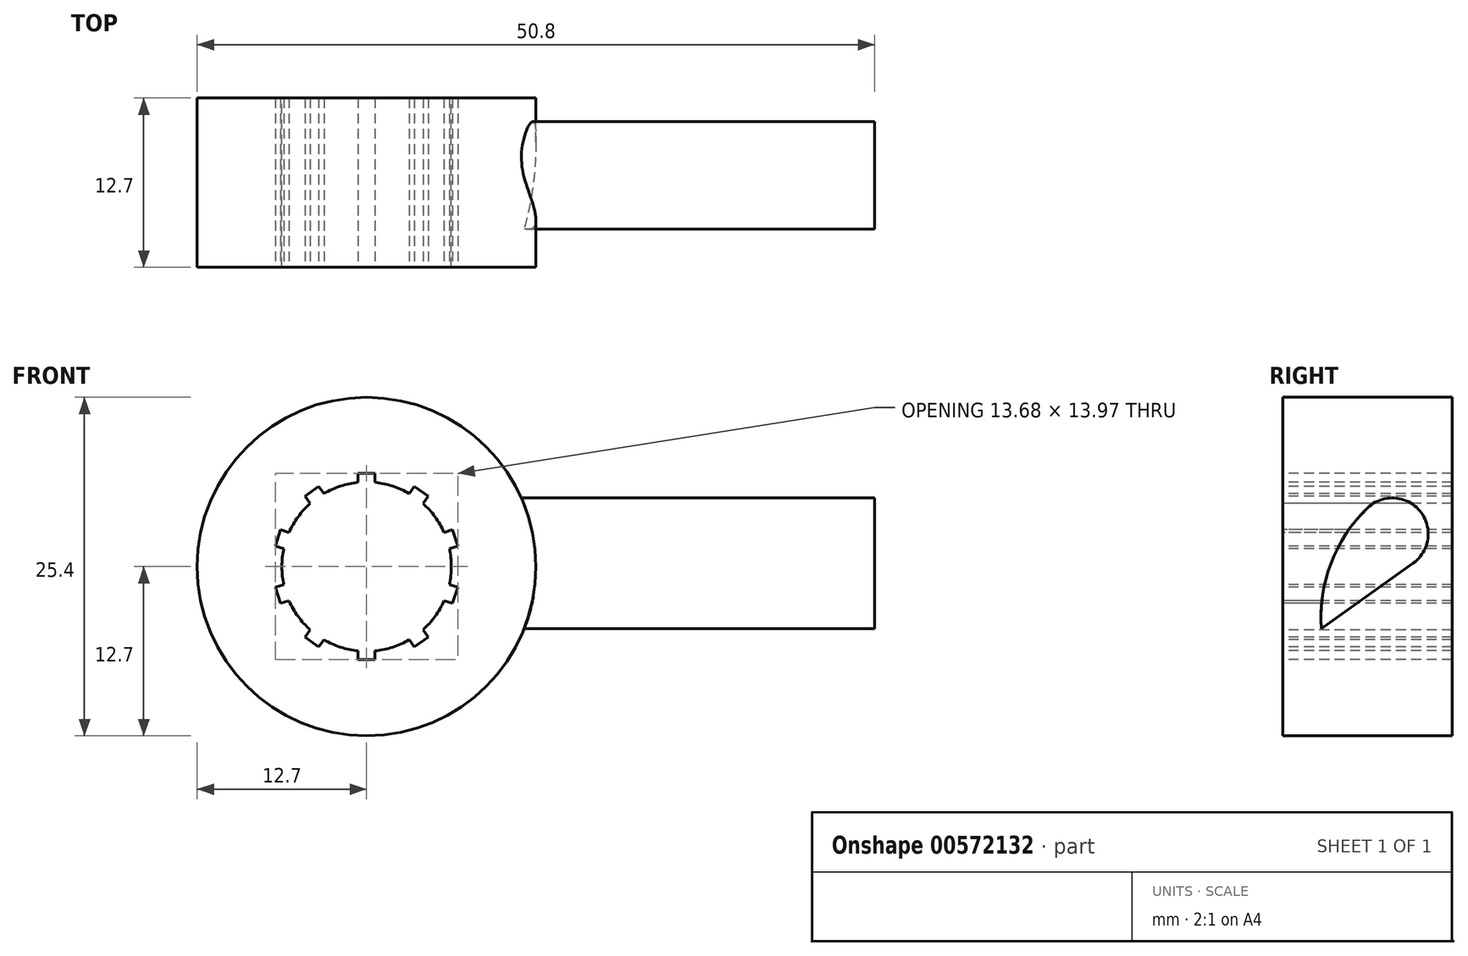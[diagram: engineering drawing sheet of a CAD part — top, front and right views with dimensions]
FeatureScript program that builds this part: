
annotation { "Feature Type Name" : "Feature", "Feature Type Description" : "" }
export const myFeature = defineFeature(function(context is Context, id is Id, definition is map)
    precondition{}
    {
        {
            var Q0;
            Q0=qCreatedBy(makeId("Front.planeOp"),FACE);
            var sketch = newSketch(context, id + "F0", { "sketchPlane" : qUnion([Q0])});
            skCircle(sketch, "E0", {"center": v(0, 0) * mm, "radius": 12.7 * mm});
            skCircle(sketch, "E1", {"center": v(0, 0) * mm, "radius": 6.35 * mm});
            skSolve(sketch);
        }
        {
            var Q0;
            Q0 = qSketchRegion(id + "F0", true);
            extrude(context, id + "F1", {"entities" : qUnion([Q0]), "endBound" : BoundingType.SYMMETRIC, "depth" : 12.7 * mm, "offsetDistance" : 25.4 * mm});
        }
        {
            var Q0;
            Q0=qCreatedBy(makeId("Front.planeOp"),FACE);
            cPlane(context, id + "F2", {"entities" : qUnion([Q0]), "cplaneType" : CPlaneType.OFFSET, "offset" : 6.35 * mm, "width" : 152.4 * mm, "height" : 152.4 * mm});
        }
        {
            var Q0;
            Q0=qCreatedBy(id+"F2.planeOp",FACE);
            var sketch = newSketch(context, id + "F3", { "sketchPlane" : qUnion([Q0])});
            skArc(sketch, "E2", {"start": v(0.63, 6.32) * mm, "mid": v(0, 6.35) * mm, "end": v(-0.64, 6.32) * mm});
            skLineSegment(sketch, "E3.bottom", {"start": v(-0.64, 6.99) * mm, "end": v(0.63, 6.99) * mm});
            skLineSegment(sketch, "E3.left", {"start": v(-0.64, 6.99) * mm, "end": v(-0.64, 6.32) * mm});
            skLineSegment(sketch, "E3.right", {"start": v(0.63, 6.99) * mm, "end": v(0.63, 6.32) * mm});
            skPoint(sketch, "E3.middle", {"position": v(0, 6.35) * mm});
            skPoint(sketch, "E3.top.start.orphan", {"position": v(-0.64, 5.72) * mm});
            skPoint(sketch, "E4.orphan", {"position": v(0.63, 5.72) * mm});
            skLineSegment(sketch, "E5.1.0", {"start": v(-3.6, 6.02) * mm, "end": v(-3.2, 5.48) * mm});
            skArc(sketch, "E5.1.1", {"start": v(-3.2, 5.48) * mm, "mid": v(-3.73, 5.14) * mm, "end": v(-4.23, 4.74) * mm});
            skLineSegment(sketch, "E5.1.2", {"start": v(-4.62, 5.28) * mm, "end": v(-4.23, 4.74) * mm});
            skLineSegment(sketch, "E5.1.3", {"start": v(-4.62, 5.28) * mm, "end": v(-3.6, 6.02) * mm});
            skLineSegment(sketch, "E5.2.0", {"start": v(-6.45, 2.76) * mm, "end": v(-5.81, 2.56) * mm});
            skArc(sketch, "E5.2.1", {"start": v(-5.81, 2.56) * mm, "mid": v(-6.04, 1.96) * mm, "end": v(-6.2, 1.35) * mm});
            skLineSegment(sketch, "E5.2.2", {"start": v(-6.84, 1.55) * mm, "end": v(-6.2, 1.35) * mm});
            skLineSegment(sketch, "E5.2.3", {"start": v(-6.84, 1.55) * mm, "end": v(-6.45, 2.76) * mm});
            skLineSegment(sketch, "E5.3.0", {"start": v(-6.84, -1.55) * mm, "end": v(-6.2, -1.35) * mm});
            skArc(sketch, "E5.3.1", {"start": v(-6.2, -1.35) * mm, "mid": v(-6.04, -1.96) * mm, "end": v(-5.81, -2.56) * mm});
            skLineSegment(sketch, "E5.3.2", {"start": v(-6.45, -2.76) * mm, "end": v(-5.81, -2.56) * mm});
            skLineSegment(sketch, "E5.3.3", {"start": v(-6.45, -2.76) * mm, "end": v(-6.84, -1.55) * mm});
            skLineSegment(sketch, "E5.4.0", {"start": v(-4.62, -5.28) * mm, "end": v(-4.23, -4.74) * mm});
            skArc(sketch, "E5.4.1", {"start": v(-4.23, -4.74) * mm, "mid": v(-3.73, -5.14) * mm, "end": v(-3.2, -5.48) * mm});
            skLineSegment(sketch, "E5.4.2", {"start": v(-3.6, -6.02) * mm, "end": v(-3.2, -5.48) * mm});
            skLineSegment(sketch, "E5.4.3", {"start": v(-3.6, -6.02) * mm, "end": v(-4.62, -5.28) * mm});
            skLineSegment(sketch, "E5.5.0", {"start": v(-0.64, -6.99) * mm, "end": v(-0.64, -6.32) * mm});
            skArc(sketch, "E5.5.1", {"start": v(-0.64, -6.32) * mm, "mid": v(0, -6.35) * mm, "end": v(0.63, -6.32) * mm});
            skLineSegment(sketch, "E5.5.2", {"start": v(0.63, -6.99) * mm, "end": v(0.63, -6.32) * mm});
            skLineSegment(sketch, "E5.5.3", {"start": v(0.63, -6.99) * mm, "end": v(-0.64, -6.99) * mm});
            skLineSegment(sketch, "E5.6.0", {"start": v(3.6, -6.02) * mm, "end": v(3.2, -5.48) * mm});
            skArc(sketch, "E5.6.1", {"start": v(3.2, -5.48) * mm, "mid": v(3.73, -5.14) * mm, "end": v(4.23, -4.74) * mm});
            skLineSegment(sketch, "E5.6.2", {"start": v(4.62, -5.28) * mm, "end": v(4.23, -4.74) * mm});
            skLineSegment(sketch, "E5.6.3", {"start": v(4.62, -5.28) * mm, "end": v(3.6, -6.02) * mm});
            skLineSegment(sketch, "E5.7.0", {"start": v(6.45, -2.76) * mm, "end": v(5.81, -2.56) * mm});
            skArc(sketch, "E5.7.1", {"start": v(5.81, -2.56) * mm, "mid": v(6.04, -1.96) * mm, "end": v(6.2, -1.35) * mm});
            skLineSegment(sketch, "E5.7.2", {"start": v(6.84, -1.55) * mm, "end": v(6.2, -1.35) * mm});
            skLineSegment(sketch, "E5.7.3", {"start": v(6.84, -1.55) * mm, "end": v(6.45, -2.76) * mm});
            skLineSegment(sketch, "E5.8.0", {"start": v(6.84, 1.55) * mm, "end": v(6.2, 1.35) * mm});
            skArc(sketch, "E5.8.1", {"start": v(6.2, 1.35) * mm, "mid": v(6.04, 1.96) * mm, "end": v(5.81, 2.56) * mm});
            skLineSegment(sketch, "E5.8.2", {"start": v(6.45, 2.76) * mm, "end": v(5.81, 2.56) * mm});
            skLineSegment(sketch, "E5.8.3", {"start": v(6.45, 2.76) * mm, "end": v(6.84, 1.55) * mm});
            skLineSegment(sketch, "E5.9.0", {"start": v(4.62, 5.28) * mm, "end": v(4.23, 4.74) * mm});
            skArc(sketch, "E5.9.1", {"start": v(4.23, 4.74) * mm, "mid": v(3.73, 5.14) * mm, "end": v(3.2, 5.48) * mm});
            skLineSegment(sketch, "E5.9.2", {"start": v(3.6, 6.02) * mm, "end": v(3.2, 5.48) * mm});
            skLineSegment(sketch, "E5.9.3", {"start": v(3.6, 6.02) * mm, "end": v(4.62, 5.28) * mm});
            skSolve(sketch);
        }
        {
            var Q0;
            Q0=makeQuery(id+"F3.imprint","IMPRINT",FACE,{"disambiguationData":[TD([[makeQuery(id+"F3.imprint","IMPRINT",EDGE,{"derivedFrom":sQuery(id+"F3.wireOp",EDGE,"E5.1.0")}),-1.0]])]});
            var Q1;
            Q1=makeQuery(id+"F3.imprint","IMPRINT",FACE,{"disambiguationData":[TD([[makeQuery(id+"F3.imprint","IMPRINT",EDGE,{"derivedFrom":sQuery(id+"F3.wireOp",EDGE,"E2")}),-1.0]])]});
            var Q2;
            Q2=makeQuery(id+"F3.imprint","IMPRINT",FACE,{"disambiguationData":[TD([[makeQuery(id+"F3.imprint","IMPRINT",EDGE,{"derivedFrom":sQuery(id+"F3.wireOp",EDGE,"E5.9.0")}),-1.0]])]});
            var Q3;
            Q3=makeQuery(id+"F3.imprint","IMPRINT",FACE,{"disambiguationData":[TD([[makeQuery(id+"F3.imprint","IMPRINT",EDGE,{"derivedFrom":sQuery(id+"F3.wireOp",EDGE,"E5.8.0")}),-1.0]])]});
            var Q4;
            Q4=makeQuery(id+"F3.imprint","IMPRINT",FACE,{"disambiguationData":[TD([[makeQuery(id+"F3.imprint","IMPRINT",EDGE,{"derivedFrom":sQuery(id+"F3.wireOp",EDGE,"E5.7.0")}),-1.0]])]});
            var Q5;
            Q5=makeQuery(id+"F3.imprint","IMPRINT",FACE,{"disambiguationData":[TD([[makeQuery(id+"F3.imprint","IMPRINT",EDGE,{"derivedFrom":sQuery(id+"F3.wireOp",EDGE,"E5.3.0")}),-1.0]])]});
            var Q6;
            Q6=makeQuery(id+"F3.imprint","IMPRINT",FACE,{"disambiguationData":[TD([[makeQuery(id+"F3.imprint","IMPRINT",EDGE,{"derivedFrom":sQuery(id+"F3.wireOp",EDGE,"E5.2.0")}),-1.0]])]});
            var Q7;
            Q7=makeQuery(id+"F3.imprint","IMPRINT",FACE,{"disambiguationData":[TD([[makeQuery(id+"F3.imprint","IMPRINT",EDGE,{"derivedFrom":sQuery(id+"F3.wireOp",EDGE,"E5.4.0")}),-1.0]])]});
            var Q8;
            Q8=makeQuery(id+"F3.imprint","IMPRINT",FACE,{"disambiguationData":[TD([[makeQuery(id+"F3.imprint","IMPRINT",EDGE,{"derivedFrom":sQuery(id+"F3.wireOp",EDGE,"E5.5.0")}),-1.0]])]});
            var Q9;
            Q9=makeQuery(id+"F3.imprint","IMPRINT",FACE,{"disambiguationData":[TD([[makeQuery(id+"F3.imprint","IMPRINT",EDGE,{"derivedFrom":sQuery(id+"F3.wireOp",EDGE,"E5.6.0")}),-1.0]])]});
            extrude(context, id + "F4", {"entities" : qUnion([Q0, Q1, Q2, Q3, Q4, Q5, Q6, Q7, Q8, Q9]), "operationType" : NewBodyOperationType.REMOVE, "oppositeDirection" : true, "depth" : 25.4 * mm, "offsetDistance" : 25.4 * mm});
        }
        {
            var Q0;
            Q0=qCreatedBy(makeId("Right.planeOp"),FACE);
            cPlane(context, id + "F5", {"entities" : qUnion([Q0]), "cplaneType" : CPlaneType.OFFSET, "offset" : 38.1 * mm, "width" : 152.4 * mm, "height" : 152.4 * mm});
        }
        {
            var Q0;
            Q0=qCreatedBy(id+"F5.planeOp",FACE);
            var sketch = newSketch(context, id + "F6", { "sketchPlane" : qUnion([Q0])});
            skPoint(sketch, "E6.middle", {"position": v(0, 0) * mm});
            skArc(sketch, "E7", {"start": v(-3.44, -4.65) * mm, "mid": v(-2.72, 0.25) * mm, "end": v(0, 4.39) * mm});
            skPoint(sketch, "E8.orphan", {"position": v(-3.44, 4.13) * mm});
            skPoint(sketch, "E6.left.start.orphan", {"position": v(-3.44, -0.26) * mm});
            skArc(sketch, "E9", {"start": v(3.44, 0.26) * mm, "mid": v(3.95, 4.18) * mm, "end": v(0, 4.39) * mm});
            skLineSegment(sketch, "E10", {"start": v(-3.44, -4.65) * mm, "end": v(3.44, 0.26) * mm});
            skPoint(sketch, "E11.orphan", {"position": v(3.44, 4.65) * mm});
            skPoint(sketch, "E12.end.orphan", {"position": v(0, -4.39) * mm});
            skPoint(sketch, "E13.orphan", {"position": v(3.44, -4.13) * mm});
            skSolve(sketch);
        }
        {
            var Q0;
            Q0 = qSketchRegion(id + "F6", true);
            extrude(context, id + "F7", {"entities" : qUnion([Q0]), "operationType" : NewBodyOperationType.ADD, "oppositeDirection" : true, "depth" : 30.48 * mm, "offsetDistance" : 25.4 * mm});
        }
    });
